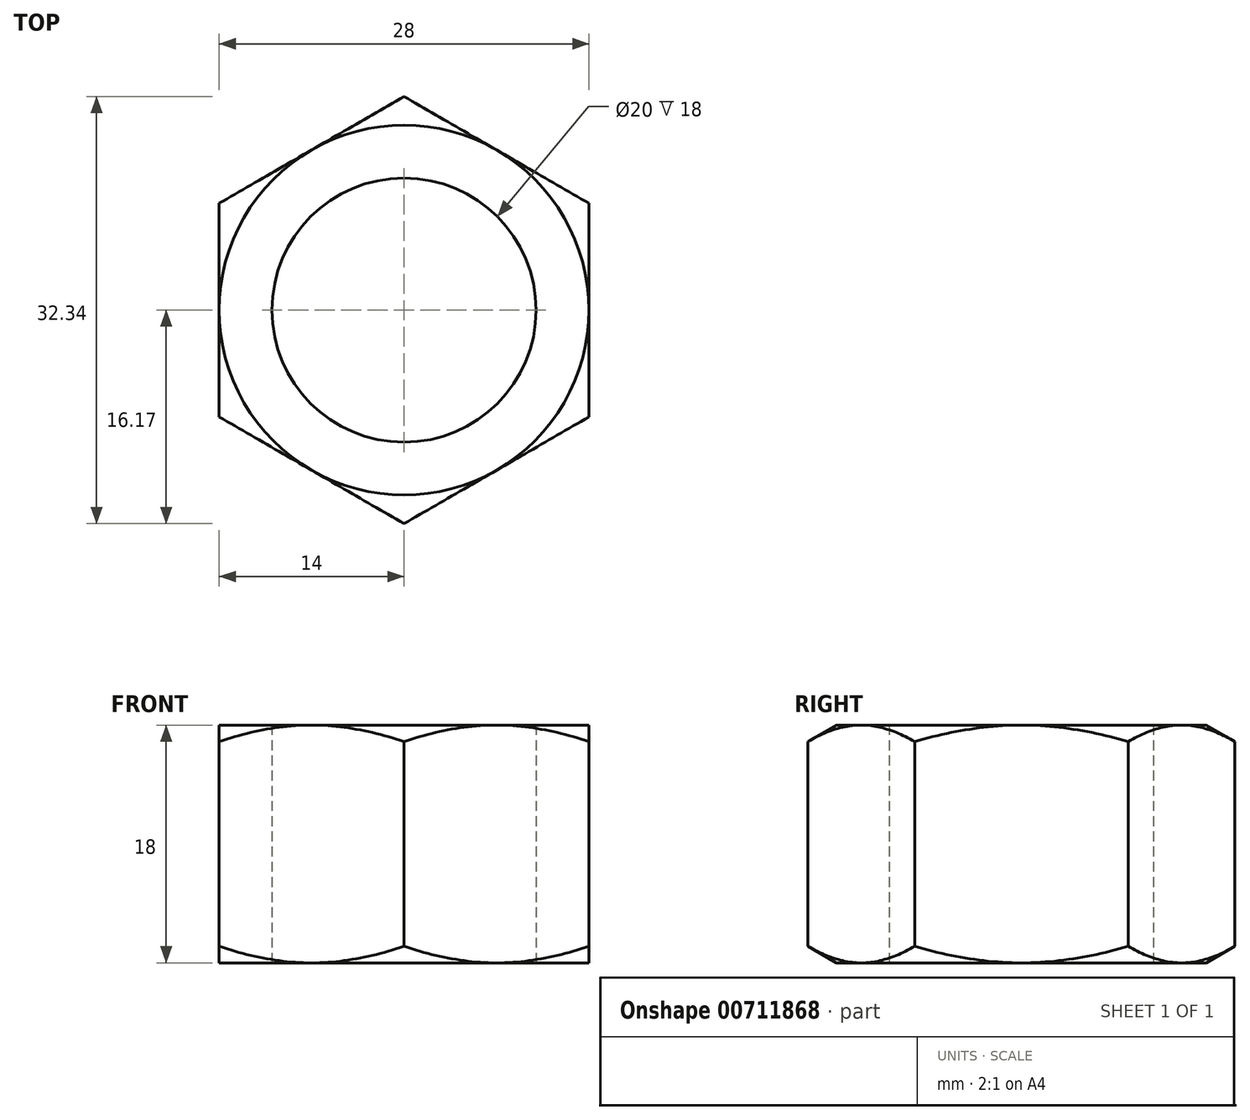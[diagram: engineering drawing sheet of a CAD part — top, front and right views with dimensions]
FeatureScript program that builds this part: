
annotation { "Feature Type Name" : "Feature", "Feature Type Description" : "" }
export const myFeature = defineFeature(function(context is Context, id is Id, definition is map)
    precondition{}
    {
        {
            var Q0;
            Q0=qCreatedBy(makeId("Top.planeOp"),FACE);
            var sketch = newSketch(context, id + "F0", { "sketchPlane" : qUnion([Q0])});
            skCircle(sketch, "E0.cCircle", {"center": v(0, 0) * mm, "radius": 14 * mm, "construction": true});
            skLineSegment(sketch, "E0.0", {"start": v(0, 16.17) * mm, "end": v(14, 8.08) * mm});
            skLineSegment(sketch, "E0.1", {"start": v(14, 8.08) * mm, "end": v(14, -8.08) * mm});
            skLineSegment(sketch, "E0.2", {"start": v(14, -8.08) * mm, "end": v(0, -16.17) * mm});
            skLineSegment(sketch, "E0.3", {"start": v(0, -16.17) * mm, "end": v(-14, -8.08) * mm});
            skLineSegment(sketch, "E0.4", {"start": v(-14, -8.08) * mm, "end": v(-14, 8.08) * mm});
            skLineSegment(sketch, "E0.5", {"start": v(-14, 8.08) * mm, "end": v(0, 16.17) * mm});
            skPoint(sketch, "E0.0.midPoint", {"position": v(7, 12.12) * mm});
            skCircle(sketch, "E1", {"center": v(0, 0) * mm, "radius": 10 * mm});
            skSolve(sketch);
        }
        {
            var Q0;
            Q0=makeQuery(id+"F0.imprint","IMPRINT",FACE,{"disambiguationData":[TD([[makeQuery(id+"F0.imprint","IMPRINT",EDGE,{"derivedFrom":sQuery(id+"F0.wireOp",EDGE,"E0.0")}),-1.0]])]});
            extrude(context, id + "F1", {"entities" : qUnion([Q0]), "depth" : 18 * mm, "offsetDistance" : 25 * mm});
        }
        {
            var Q0;
            Q0=qCreatedBy(makeId("Front.planeOp"),FACE);
            var sketch = newSketch(context, id + "F2", { "sketchPlane" : qUnion([Q0])});
            skLineSegment(sketch, "E2", {"start": v(0, 0) * mm, "end": v(0, 18) * mm, "construction": true});
            skLineSegment(sketch, "E3", {"start": v(0, 9) * mm, "end": v(10.35, 9) * mm, "construction": true});
            skLineSegment(sketch, "E4", {"start": v(14, 18) * mm, "end": v(22.7, 18) * mm});
            skLineSegment(sketch, "E5", {"start": v(22.7, 18) * mm, "end": v(22.7, 12.98) * mm});
            skLineSegment(sketch, "E6", {"start": v(22.7, 12.98) * mm, "end": v(14, 18) * mm});
            skLineSegment(sketch, "E7.MirrorCS", {"start": v(14, 0) * mm, "end": v(22.7, 0) * mm});
            skLineSegment(sketch, "E8.MirrorCS", {"start": v(22.7, 5.02) * mm, "end": v(14, 0) * mm});
            skLineSegment(sketch, "E9.MirrorCS", {"start": v(22.7, 0) * mm, "end": v(22.7, 5.02) * mm});
            skSolve(sketch);
        }
        {
            var Q0;
            Q0 = qSketchRegion(id + "F2", true);
            var Q1;
            Q1=sQuery(id+"F2.wireOp",EDGE,"E2");
            revolve(context, id + "F3", {"operationType" : NewBodyOperationType.REMOVE, "surfaceOperationType" : NewSurfaceOperationType.NEW, "entities" : qUnion([Q0]), "axis" : qUnion([Q1]), "revolveType" : RevolveType.FULL, "oppositeDirection" : true});
        }
    });
